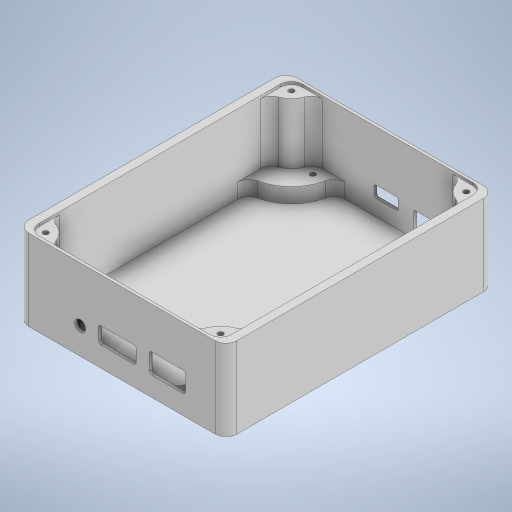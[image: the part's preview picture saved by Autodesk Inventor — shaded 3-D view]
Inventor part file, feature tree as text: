
AUTODESK INVENTOR PART (.ipt)
format: ipt  version: 2024 (Build 280153000, 153)  size: 679,424 bytes
history: native  units: mm
features: other x44, projected_geometry x7, sketch x6, extrude x6, hole x2
ambient origin geometry x8: Origin, YZ Plane, XZ Plane, XY Plane, X Axis, Y Axis, Z Axis, Center Point
bodies: 实体1 (feature_tree)
feature tree (65):
  sketch  "草图1"  dims[d0=122.78mm d1=95.4mm]
  extrude  "拉伸1"  Depth=95.4mm
  extrude  "拉伸2"  Depth=88.0mm
  extrude  "拉伸3"  TaperAngle=90.0deg  [1 undecoded]
  extrude  "拉伸4"  TaperAngle=90.0deg  [1 undecoded]
  hole  "孔3"  [1 undecoded]
  hole  "孔5"  [1 undecoded]
  other  "面圆角1"
  other  "面圆角2"
  other  "面圆角3"
  other  "面圆角4"
  other  "面圆角5"
  other  "面圆角6"
  other  "面圆角7"
  other  "面圆角8"
  other  "面圆角9"
  other  "面圆角10"
  other  "面圆角11"
  other  "面圆角12"
  other  "面圆角13"
  other  "面圆角14"
  other  "面圆角15"
  other  "面圆角16"
  other  "面圆角17"
  other  "面圆角18"
  other  "面圆角19"
  other  "面圆角20"
  other  "面圆角21"
  other  "面圆角22"
  other  "面圆角23"
  other  "面圆角24"
  extrude  "拉伸5"  Depth=1.0mm
  other  "面圆角25"
  other  "面圆角26"
  other  "面圆角27"
  other  "面圆角28"
  other  "面圆角29"
  other  "面圆角30"
  other  "面圆角31"
  other  "面圆角32"
  sketch  "草图8"  dims[d8=55.88mm d9=29.848mm]
  extrude  "拉伸6"  Depth=1.0mm
  other  "面圆角33"
  other  "面圆角34"
  other  "面圆角35"
  other  "面圆角36"
  other  "面圆角37"
  other  "面圆角38"
  other  "面圆角39"
  other  "面圆角40"
  sketch  "草图3"  dims[d2=120.38mm d3=88.0mm]
  sketch  "草图6"  dims[d4=20.0mm d5=90.0deg]
  projected_geometry  "投影回路6"
  sketch  "草图7"  dims[d6=10.0mm d7=90.0deg]
  projected_geometry  "投影回路7"
  projected_geometry  "投影回路8"
  projected_geometry  "投影回路9"
  sketch  "草图9"  dims[d10=4.0mm d11=4.0mm d12=2.5mm d13=2.5mm d14=37.0mm d15=0.0mm d16=1.2mm d17=0.0mm d18=8.0mm d19=0.0mm d20=35.8mm d21=0.0mm d36=2.459mm d37=6.0mm d38=4.0mm d39=2.0mm d40=90.0deg d41=6.0mm d42=20.594885mm d50=4.0mm d51=4.0mm d52=2.459mm d53=6.0mm d54=4.0mm d55=2.0mm d56=90.0deg d57=6.0mm d58=20.594885mm d59=5.0mm d60=5.0mm d61=5.0mm d62=5.0mm d63=5.0mm d64=5.0mm d65=5.0mm d66=5.0mm d67=5.0mm d68=5.0mm d69=5.0mm d70=5.0mm d71=5.0mm d72=5.0mm d73=5.0mm d74=5.0mm d75=5.0mm d76=5.0mm d77=5.0mm d78=5.0mm d79=5.0mm d80=5.0mm d81=5.0mm d82=5.0mm d84=1.6mm d85=18.415mm d86=0.95mm d87=10.05mm d88=16.4mm d89=4.445mm d90=1.3mm d91=8.85mm d92=17.1mm d93=21.463mm d94=4.1mm d95=5.0mm d96=20.0mm d97=0.0mm d98=1.0mm d99=1.0mm d100=1.0mm d101=1.0mm d102=1.0mm d103=1.0mm d104=1.0mm d105=1.0mm d106=1.6mm d107=0.8mm d108=19.177mm d109=3.94mm d110=5.26mm d111=7.125mm d112=7.125mm d113=0.635mm d114=1.65mm d115=11.0mm d116=5.3mm d117=20.0mm d118=0.0mm d119=1.0mm d120=1.0mm d121=1.0mm d122=1.0mm d123=1.0mm d124=1.0mm d125=1.0mm d126=1.0mm d22=1.0mm d23=1.0mm d24=6.5mm d25=0.15mm d26=3.0mm d27=0.375mm d28=14.3117mm d29=6.0mm d30=20.594885mm d31=0.0625mm d32=0.75mm d33=0.375mm d43=0.75mm d44=20.594885mm d45=0.0625mm d46=0.75mm d47=0.375mm]
  projected_geometry  "投影回路10"
  projected_geometry  "投影回路11"
  projected_geometry  "投影回路12"
  other  "投影剖切边1"
  other  "投影剖切边2"
  other  "投影剖切边16"
  other  "投影剖切边17"
note: 4 required parameter values undecoded (feature->parameter linkage not recoverable at this tier; creation-order binding heuristic only, values carry confidence <= 0.55)
